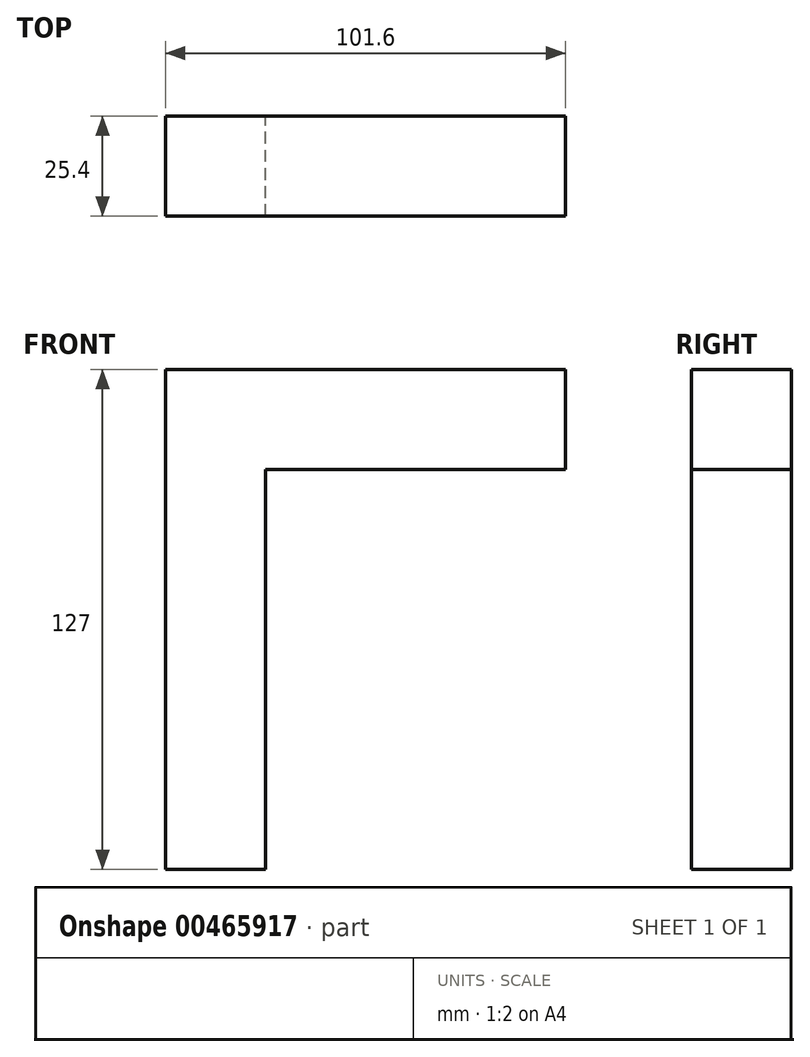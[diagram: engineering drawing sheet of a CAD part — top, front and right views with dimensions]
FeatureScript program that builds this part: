
annotation { "Feature Type Name" : "Feature", "Feature Type Description" : "" }
export const myFeature = defineFeature(function(context is Context, id is Id, definition is map)
    precondition{}
    {
        {
            var Q0;
            Q0=qCreatedBy(makeId("Front.planeOp"),FACE);
            var sketch = newSketch(context, id + "F0", { "sketchPlane" : qUnion([Q0])});
            skLineSegment(sketch, "E0.bottom", {"start": v(-50.8, 63.5) * mm, "end": v(50.8, 63.5) * mm});
            skLineSegment(sketch, "E0.top", {"start": v(-50.8, -63.5) * mm, "end": v(50.8, -63.5) * mm});
            skLineSegment(sketch, "E0.left", {"start": v(-50.8, 63.5) * mm, "end": v(-50.8, -63.5) * mm});
            skLineSegment(sketch, "E0.right", {"start": v(50.8, 63.5) * mm, "end": v(50.8, -63.5) * mm});
            skPoint(sketch, "E0.middle", {"position": v(0, 0) * mm});
            skLineSegment(sketch, "E1.bottom", {"start": v(50.8, -63.5) * mm, "end": v(-25.4, -63.5) * mm});
            skLineSegment(sketch, "E1.top", {"start": v(50.8, 38.1) * mm, "end": v(-25.4, 38.1) * mm});
            skLineSegment(sketch, "E1.left", {"start": v(50.8, -63.5) * mm, "end": v(50.8, 38.1) * mm});
            skLineSegment(sketch, "E1.right", {"start": v(-25.4, -63.5) * mm, "end": v(-25.4, 38.1) * mm});
            skSolve(sketch);
        }
        {
            var Q0;
            Q0=makeQuery(id+"F0.imprint","IMPRINT",FACE,{"disambiguationData":[TD([[makeQuery(id+"F0.imprint","IMPRINT",EDGE,{"derivedFrom":sQuery(id+"F0.wireOp",EDGE,"E0.bottom")}),-1.0]])]});
            extrude(context, id + "F1", {"entities" : qUnion([Q0]), "endBound" : BoundingType.SYMMETRIC, "depth" : 25.4 * mm});
        }
    });
